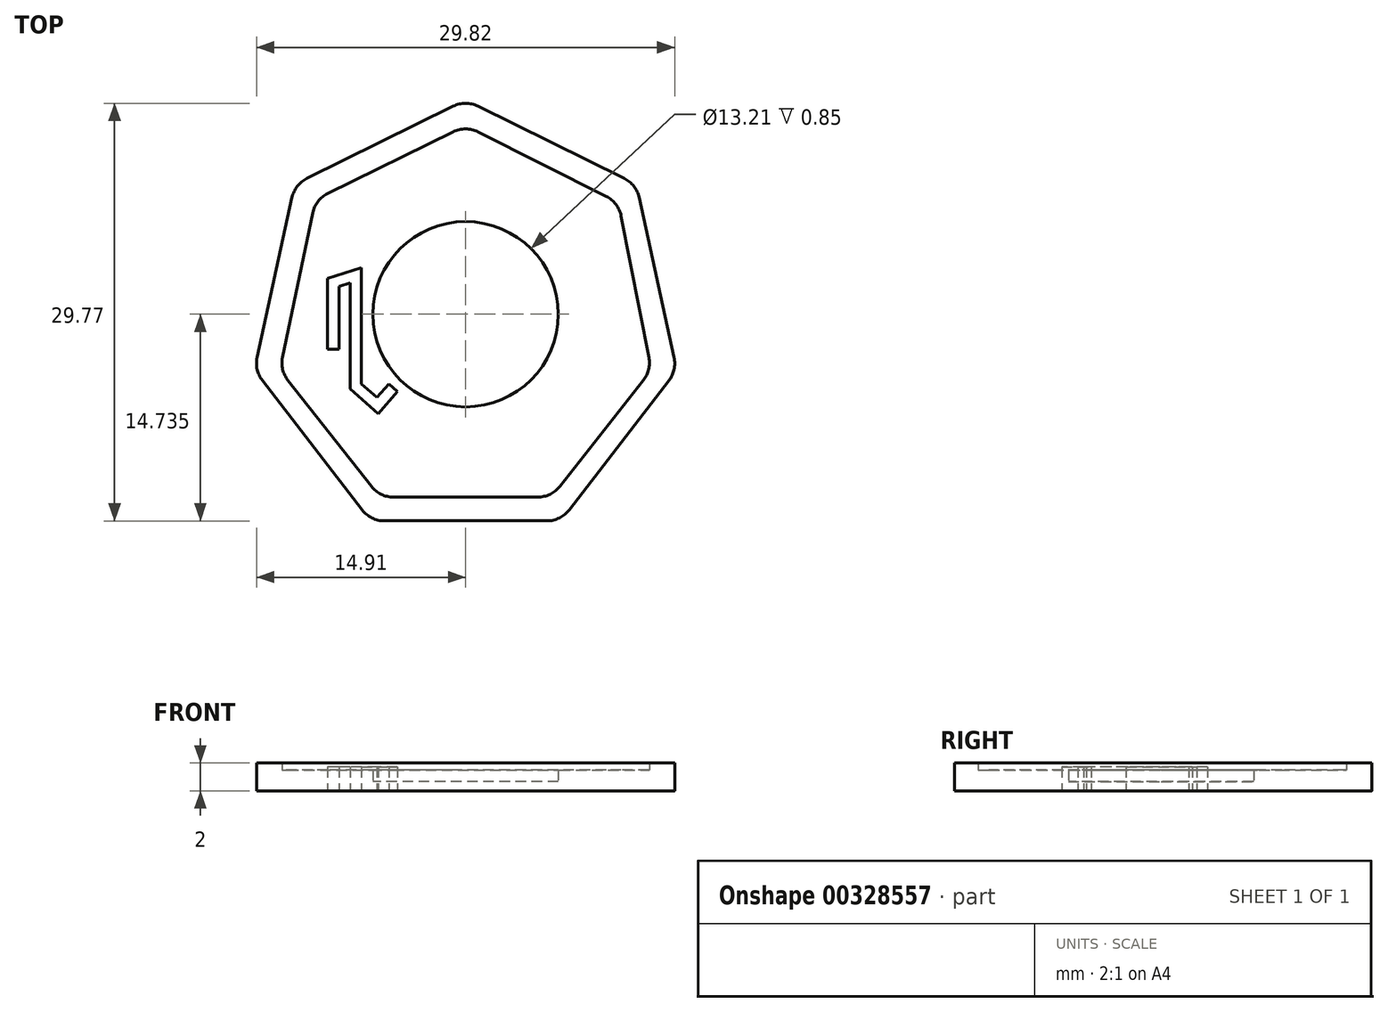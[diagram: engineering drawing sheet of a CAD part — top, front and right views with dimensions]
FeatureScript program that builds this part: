
annotation { "Feature Type Name" : "Feature", "Feature Type Description" : "" }
export const myFeature = defineFeature(function(context is Context, id is Id, definition is map)
    precondition{}
    {
        {
            var Q0;
            Q0=qCreatedBy(makeId("Top.planeOp"),FACE);
            var sketch = newSketch(context, id + "F0", { "sketchPlane" : qUnion([Q0])});
            skLineSegment(sketch, "E0", {"start": v(5.8, -10.75) * mm, "end": v(-5.8, -10.75) * mm});
            skLineSegment(sketch, "E1", {"start": v(7.38, -9.97) * mm, "end": v(14.5, -0.74) * mm});
            skLineSegment(sketch, "E2", {"start": v(-7.38, -9.97) * mm, "end": v(-14.5, -0.74) * mm});
            skLineSegment(sketch, "E3", {"start": v(-12.37, 12.31) * mm, "end": v(-14.86, 0.9) * mm});
            skLineSegment(sketch, "E4", {"start": v(12.37, 12.31) * mm, "end": v(14.86, 0.9) * mm});
            skLineSegment(sketch, "E5", {"start": v(-0.88, 18.82) * mm, "end": v(-11.3, 13.68) * mm});
            skLineSegment(sketch, "E6", {"start": v(0.88, 18.82) * mm, "end": v(11.3, 13.68) * mm});
            skLineSegment(sketch, "E7", {"start": v(-0.9, 17) * mm, "end": v(-9.83, 12.6) * mm});
            skLineSegment(sketch, "E8", {"start": v(-10.9, 11.22) * mm, "end": v(-13.05, 0.91) * mm});
            skLineSegment(sketch, "E9", {"start": v(13.07, 0.9) * mm, "end": v(11.09, 10.99) * mm});
            skLineSegment(sketch, "E10", {"start": v(10.02, 12.4) * mm, "end": v(0.89, 16.99) * mm});
            skLineSegment(sketch, "E11", {"start": v(-12.17, 13.25) * mm, "end": v(-10.7, 12.17) * mm, "construction": true});
            skLineSegment(sketch, "E12", {"start": v(12.17, 13.25) * mm, "end": v(10.9, 11.95) * mm, "construction": true});
            skLineSegment(sketch, "E13", {"start": v(0, 19.25) * mm, "end": v(0, 17.43) * mm, "construction": true});
            skLineSegment(sketch, "E14", {"start": v(-15.06, 0) * mm, "end": v(-13.24, 0) * mm, "construction": true});
            skLineSegment(sketch, "E15", {"start": v(13.24, 0) * mm, "end": v(15.06, 0) * mm, "construction": true});
            skLineSegment(sketch, "E16", {"start": v(-12.67, -0.73) * mm, "end": v(-6.72, -8.3) * mm});
            skLineSegment(sketch, "E17", {"start": v(-5.15, -9.05) * mm, "end": v(5.15, -9.05) * mm});
            skLineSegment(sketch, "E18", {"start": v(6.72, -8.3) * mm, "end": v(12.68, -0.72) * mm});
            skLineSegment(sketch, "E19", {"start": v(-6.12, -9.05) * mm, "end": v(-6.78, -10.75) * mm, "construction": true});
            skLineSegment(sketch, "E20", {"start": v(6.12, -9.05) * mm, "end": v(6.78, -10.75) * mm, "construction": true});
            skPoint(sketch, "E21", {"position": v(0, -10.75) * mm});
            skPoint(sketch, "E22.visualSharp", {"position": v(0, 17.43) * mm});
            skArc(sketch, "E22.filletArc", {"start": v(0.89, 16.99) * mm, "mid": v(0, 17.2) * mm, "end": v(-0.9, 17) * mm});
            skPoint(sketch, "E23.visualSharp", {"position": v(10.9, 11.95) * mm});
            skArc(sketch, "E23.filletArc", {"start": v(11.09, 10.99) * mm, "mid": v(10.72, 11.81) * mm, "end": v(10.02, 12.4) * mm});
            skPoint(sketch, "E24.visualSharp", {"position": v(13.24, 0) * mm});
            skArc(sketch, "E24.filletArc", {"start": v(12.68, -0.72) * mm, "mid": v(13.05, 0.05) * mm, "end": v(13.07, 0.9) * mm});
            skPoint(sketch, "E25.visualSharp", {"position": v(-6.12, -9.05) * mm});
            skArc(sketch, "E25.filletArc", {"start": v(-6.72, -8.3) * mm, "mid": v(-6.02, -8.85) * mm, "end": v(-5.15, -9.05) * mm});
            skPoint(sketch, "E26.visualSharp", {"position": v(6.12, -9.05) * mm});
            skArc(sketch, "E26.filletArc", {"start": v(5.15, -9.05) * mm, "mid": v(6.02, -8.85) * mm, "end": v(6.72, -8.3) * mm});
            skPoint(sketch, "E27.visualSharp", {"position": v(-13.24, 0) * mm});
            skArc(sketch, "E27.filletArc", {"start": v(-13.05, 0.91) * mm, "mid": v(-13.04, 0.05) * mm, "end": v(-12.67, -0.73) * mm});
            skPoint(sketch, "E28.visualSharp", {"position": v(-10.7, 12.17) * mm});
            skArc(sketch, "E28.filletArc", {"start": v(-9.83, 12.6) * mm, "mid": v(-10.53, 12.03) * mm, "end": v(-10.9, 11.22) * mm});
            skPoint(sketch, "E29.visualSharp", {"position": v(0, 19.25) * mm});
            skArc(sketch, "E29.filletArc", {"start": v(0.88, 18.82) * mm, "mid": v(0, 19.02) * mm, "end": v(-0.88, 18.82) * mm});
            skPoint(sketch, "E30.visualSharp", {"position": v(-12.17, 13.25) * mm});
            skArc(sketch, "E30.filletArc", {"start": v(-11.3, 13.68) * mm, "mid": v(-12, 13.12) * mm, "end": v(-12.37, 12.31) * mm});
            skPoint(sketch, "E31.visualSharp", {"position": v(-15.06, 0) * mm});
            skArc(sketch, "E31.filletArc", {"start": v(-14.86, 0.9) * mm, "mid": v(-14.86, 0.05) * mm, "end": v(-14.5, -0.74) * mm});
            skPoint(sketch, "E32.visualSharp", {"position": v(-6.78, -10.75) * mm});
            skArc(sketch, "E32.filletArc", {"start": v(-7.38, -9.97) * mm, "mid": v(-6.68, -10.54) * mm, "end": v(-5.8, -10.75) * mm});
            skPoint(sketch, "E33.visualSharp", {"position": v(6.78, -10.75) * mm});
            skArc(sketch, "E33.filletArc", {"start": v(5.8, -10.75) * mm, "mid": v(6.68, -10.54) * mm, "end": v(7.38, -9.97) * mm});
            skPoint(sketch, "E34.visualSharp", {"position": v(15.06, 0) * mm});
            skArc(sketch, "E34.filletArc", {"start": v(14.5, -0.74) * mm, "mid": v(14.86, 0.05) * mm, "end": v(14.86, 0.9) * mm});
            skPoint(sketch, "E35.visualSharp", {"position": v(12.17, 13.25) * mm});
            skArc(sketch, "E35.filletArc", {"start": v(12.37, 12.31) * mm, "mid": v(12, 13.12) * mm, "end": v(11.3, 13.68) * mm});
            skPoint(sketch, "E36", {"position": v(0, -9.05) * mm});
            skLineSegment(sketch, "E37", {"start": v(0, 17.02) * mm, "end": v(0, -9.05) * mm, "construction": true});
            skPoint(sketch, "E38", {"position": v(0, 3.98) * mm});
            skPoint(sketch, "E39", {"position": v(0, -2.53) * mm});
            skPoint(sketch, "E40", {"position": v(0, 10.5) * mm});
            skCircle(sketch, "E41", {"center": v(0, 3.98) * mm, "radius": 6.6 * mm});
            skSolve(sketch);
        }
        {
            var Q0;
            Q0=makeQuery(id+"F0.imprint","IMPRINT",FACE,{"disambiguationData":[TD([[makeQuery(id+"F0.imprint","IMPRINT",EDGE,{"derivedFrom":sQuery(id+"F0.wireOp",EDGE,"E7")}),1.0]])]});
            extrude(context, id + "F1", {"entities" : qUnion([Q0]), "depth" : 1.5 * mm});
        }
        {
            var Q0;
            Q0=makeQuery(id+"F0.imprint","IMPRINT",FACE,{"disambiguationData":[TD([[makeQuery(id+"F0.imprint","IMPRINT",EDGE,{"derivedFrom":sQuery(id+"F0.wireOp",EDGE,"E3")}),1.0]])]});
            var Q1;
            Q1=makeQuery(id+"F0.imprint","IMPRINT",FACE,{"disambiguationData":[TD([[makeQuery(id+"F0.imprint","IMPRINT",EDGE,{"derivedFrom":sQuery(id+"F0.wireOp",EDGE,"E5")}),1.0]])]});
            var Q2;
            Q2=makeQuery(id+"F0.imprint","IMPRINT",FACE,{"disambiguationData":[TD([[makeQuery(id+"F0.imprint","IMPRINT",EDGE,{"derivedFrom":sQuery(id+"F0.wireOp",EDGE,"E6")}),-1.0]])]});
            var Q3;
            Q3=makeQuery(id+"F0.imprint","IMPRINT",FACE,{"disambiguationData":[TD([[makeQuery(id+"F0.imprint","IMPRINT",EDGE,{"derivedFrom":sQuery(id+"F0.wireOp",EDGE,"E4")}),-1.0]])]});
            var Q4;
            Q4=makeQuery(id+"F0.imprint","IMPRINT",FACE,{"disambiguationData":[TD([[makeQuery(id+"F0.imprint","IMPRINT",EDGE,{"derivedFrom":sQuery(id+"F0.wireOp",EDGE,"E1")}),1.0]])]});
            var Q5;
            Q5=makeQuery(id+"F0.imprint","IMPRINT",FACE,{"disambiguationData":[TD([[makeQuery(id+"F0.imprint","IMPRINT",EDGE,{"derivedFrom":sQuery(id+"F0.wireOp",EDGE,"E0")}),-1.0]])]});
            var Q6;
            Q6=makeQuery(id+"F0.imprint","IMPRINT",FACE,{"disambiguationData":[TD([[makeQuery(id+"F0.imprint","IMPRINT",EDGE,{"derivedFrom":sQuery(id+"F0.wireOp",EDGE,"E2")}),-1.0]])]});
            extrude(context, id + "F2", {"entities" : qUnion([Q0, Q1, Q2, Q3, Q4, Q5, Q6]), "operationType" : NewBodyOperationType.ADD, "depth" : 2 * mm});
        }
        {
            var Q0;
            Q0=makeQuery(id+"F0.imprint","IMPRINT",FACE,{"disambiguationData":[TD([[makeQuery(id+"F0.imprint","IMPRINT",EDGE,{"derivedFrom":sQuery(id+"F0.wireOp",EDGE,"E41")}),1.0]])]});
            extrude(context, id + "F3", {"entities" : qUnion([Q0]), "operationType" : NewBodyOperationType.ADD, "depth" : 0.65 * mm});
        }
        {
            var Q0;
            Q0=qCreatedBy(makeId("Top.planeOp"),FACE);
            var sketch = newSketch(context, id + "F4", { "sketchPlane" : qUnion([Q0])});
            skLineSegment(sketch, "E42.0", {"start": v(-10.9, 11.22) * mm, "end": v(-13.05, 0.91) * mm});
            skArc(sketch, "E42.1", {"start": v(-9.83, 12.6) * mm, "mid": v(-10.53, 12.03) * mm, "end": v(-10.9, 11.22) * mm});
            skLineSegment(sketch, "E42.2", {"start": v(-0.9, 17) * mm, "end": v(-9.83, 12.6) * mm});
            skArc(sketch, "E42.3", {"start": v(0.89, 16.99) * mm, "mid": v(0, 17.2) * mm, "end": v(-0.9, 17) * mm});
            skLineSegment(sketch, "E42.4", {"start": v(10.02, 12.4) * mm, "end": v(0.89, 16.99) * mm});
            skLineSegment(sketch, "E42.5", {"start": v(13.07, 0.9) * mm, "end": v(11.09, 10.99) * mm});
            skArc(sketch, "E42.6", {"start": v(12.68, -0.72) * mm, "mid": v(13.05, 0.05) * mm, "end": v(13.07, 0.9) * mm});
            skLineSegment(sketch, "E42.7", {"start": v(6.72, -8.3) * mm, "end": v(12.68, -0.72) * mm});
            skArc(sketch, "E42.8", {"start": v(11.09, 10.99) * mm, "mid": v(10.72, 11.81) * mm, "end": v(10.02, 12.4) * mm});
            skArc(sketch, "E42.9", {"start": v(-13.05, 0.91) * mm, "mid": v(-13.04, 0.05) * mm, "end": v(-12.67, -0.73) * mm});
            skLineSegment(sketch, "E42.10", {"start": v(-12.67, -0.73) * mm, "end": v(-6.72, -8.3) * mm});
            skArc(sketch, "E42.11", {"start": v(-6.72, -8.3) * mm, "mid": v(-6.02, -8.85) * mm, "end": v(-5.15, -9.05) * mm});
            skLineSegment(sketch, "E42.12", {"start": v(-5.15, -9.05) * mm, "end": v(5.15, -9.05) * mm});
            skArc(sketch, "E42.13", {"start": v(5.15, -9.05) * mm, "mid": v(6.02, -8.85) * mm, "end": v(6.72, -8.3) * mm});
            skCircle(sketch, "E42.14", {"center": v(0, 3.98) * mm, "radius": 6.6 * mm});
            skLineSegment(sketch, "E43", {"start": v(0, 10.6) * mm, "end": v(0, -2.62) * mm});
            skPoint(sketch, "E44", {"position": v(0, 0.68) * mm});
            skPoint(sketch, "E45", {"position": v(0, -0.97) * mm});
            skPoint(sketch, "E46", {"position": v(-4.37, -0.97) * mm});
            skLineSegment(sketch, "E47", {"start": v(-5.25, -1.97) * mm, "end": v(-6.24, -3.1) * mm});
            skLineSegment(sketch, "E48", {"start": v(-7.9, -1.64) * mm, "end": v(-6.24, -3.1) * mm});
            skPoint(sketch, "E49", {"position": v(-4.86, -1.53) * mm});
            skLineSegment(sketch, "E50", {"start": v(-5.01, -1.4) * mm, "end": v(-5.32, -1.13) * mm});
            skLineSegment(sketch, "E51", {"start": v(-5.85, -1.43) * mm, "end": v(-6.31, -1.95) * mm});
            skLineSegment(sketch, "E52", {"start": v(-7.36, -1.03) * mm, "end": v(-6.31, -1.95) * mm});
            skPoint(sketch, "E53", {"position": v(0, 7.3) * mm});
            skLineSegment(sketch, "E54", {"start": v(-7.42, -0.88) * mm, "end": v(-7.42, 7.3) * mm});
            skLineSegment(sketch, "E55", {"start": v(-9.03, 5.82) * mm, "end": v(-9.03, 1.7) * mm});
            skLineSegment(sketch, "E56", {"start": v(-9.84, 6.4) * mm, "end": v(-9.84, 1.7) * mm});
            skLineSegment(sketch, "E57", {"start": v(-7.42, 7.3) * mm, "end": v(-9.7, 6.6) * mm});
            skLineSegment(sketch, "E58", {"start": v(-8.89, 6.01) * mm, "end": v(-8.24, 6.21) * mm});
            skLineSegment(sketch, "E59", {"start": v(-9.64, 1.5) * mm, "end": v(-9.23, 1.5) * mm});
            skPoint(sketch, "E60.end.orphan", {"position": v(0, 6.55) * mm});
            skLineSegment(sketch, "E61.trimOffspring", {"start": v(-8.24, 6.21) * mm, "end": v(-8.24, -0.89) * mm});
            skPoint(sketch, "E62.orphan", {"position": v(-5.7, -2.49) * mm});
            skPoint(sketch, "E63.visualSharp", {"position": v(-9.84, 1.5) * mm});
            skPoint(sketch, "E64.visualSharp", {"position": v(-9.03, 1.5) * mm});
            skPoint(sketch, "E65.visualSharp", {"position": v(-7.42, -0.97) * mm});
            skPoint(sketch, "E66.visualSharp", {"position": v(-5.47, -1) * mm});
            skPoint(sketch, "E67.visualSharp", {"position": v(-9.03, 5.97) * mm});
            skPoint(sketch, "E68.visualSharp", {"position": v(-9.84, 6.55) * mm});
            skLineSegment(sketch, "E69", {"start": v(-5.85, -1.43) * mm, "end": v(-5.47, -1) * mm});
            skLineSegment(sketch, "E70", {"start": v(-5.32, -1.13) * mm, "end": v(-5.47, -1) * mm});
            skLineSegment(sketch, "E71", {"start": v(-5.01, -1.4) * mm, "end": v(-4.86, -1.53) * mm});
            skLineSegment(sketch, "E72", {"start": v(-5.25, -1.97) * mm, "end": v(-4.86, -1.53) * mm});
            skLineSegment(sketch, "E73", {"start": v(-7.36, -1.03) * mm, "end": v(-7.42, -0.97) * mm});
            skLineSegment(sketch, "E74", {"start": v(-7.42, -0.88) * mm, "end": v(-7.42, -0.97) * mm});
            skLineSegment(sketch, "E75", {"start": v(-9.7, 6.6) * mm, "end": v(-9.84, 6.55) * mm});
            skLineSegment(sketch, "E76", {"start": v(-9.84, 6.4) * mm, "end": v(-9.84, 6.55) * mm});
            skLineSegment(sketch, "E77", {"start": v(-8.89, 6.01) * mm, "end": v(-9.03, 5.97) * mm});
            skLineSegment(sketch, "E78", {"start": v(-9.03, 5.82) * mm, "end": v(-9.03, 5.97) * mm});
            skLineSegment(sketch, "E79", {"start": v(-9.84, 1.7) * mm, "end": v(-9.84, 1.5) * mm});
            skLineSegment(sketch, "E80", {"start": v(-9.64, 1.5) * mm, "end": v(-9.03, 1.5) * mm});
            skLineSegment(sketch, "E81", {"start": v(-9.03, 1.7) * mm, "end": v(-9.03, 1.5) * mm});
            skLineSegment(sketch, "E82", {"start": v(-9.64, 1.5) * mm, "end": v(-9.84, 1.5) * mm});
            skLineSegment(sketch, "E83", {"start": v(-7.9, -1.64) * mm, "end": v(-8.24, -1.34) * mm});
            skLineSegment(sketch, "E84", {"start": v(-8.24, -0.89) * mm, "end": v(-8.24, -1.34) * mm});
            skLineSegment(sketch, "E85", {"start": v(-6.24, -3.1) * mm, "end": v(-9.21, -3.1) * mm});
            skSolve(sketch);
        }
        {
            var Q0;
            {var subQ1=sQuery(id+"F4.wireOp",EDGE,"E54");Q0=makeQuery(id+"F4.imprint","IMPRINT",FACE,{"disambiguationData":[TD([[makeQuery(id+"F4.imprint","IMPRINT",EDGE,{"derivedFrom":subQ1}),1.0]])]});}
            var Q1;
            Q1=makeQuery(id+"F4.imprint","IMPRINT",FACE,{"disambiguationData":[TD([[makeQuery(id+"F4.imprint","IMPRINT",EDGE,{"derivedFrom":sQuery(id+"F4.wireOp",EDGE,"E47")}),-1.0]])]});
            var Q2;
            Q2=makeQuery(id+"F4.imprint","IMPRINT",FACE,{"disambiguationData":[TD([[makeQuery(id+"F4.imprint","IMPRINT",EDGE,{"derivedFrom":sQuery(id+"F4.wireOp",EDGE,"7975e69f-e4dc-4e5e-a89b-88cfc07297f20.MirrorCS")}),1.0]])]});
            extrude(context, id + "F5", {"entities" : qUnion([Q0, Q1, Q2]), "depth" : 1.7 * mm});
        }
    });
